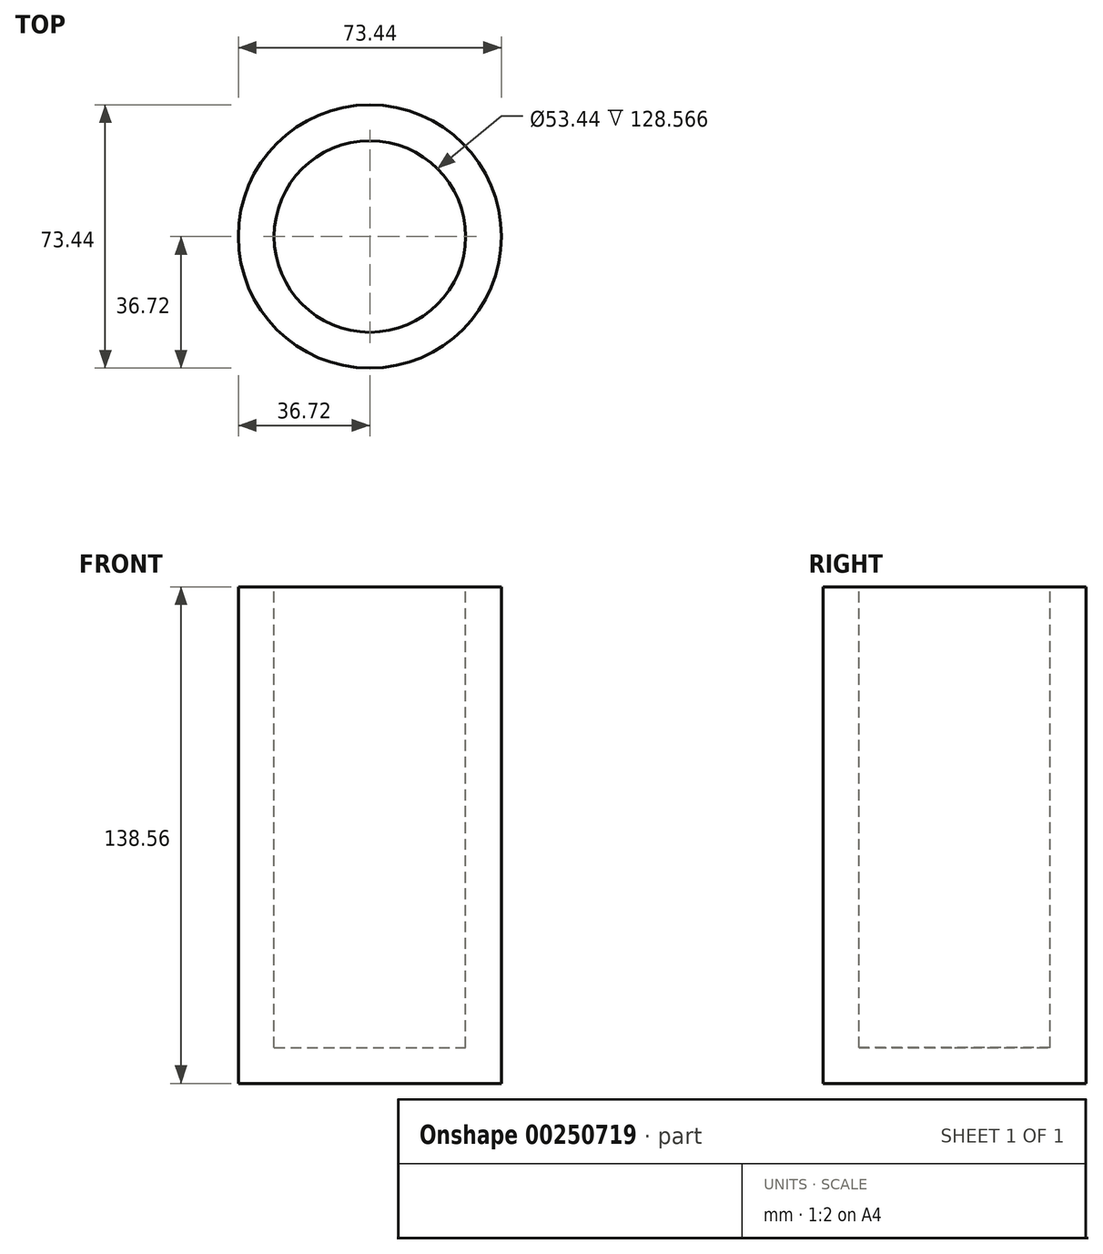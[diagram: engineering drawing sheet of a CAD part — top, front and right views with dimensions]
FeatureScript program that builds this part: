
annotation { "Feature Type Name" : "Feature", "Feature Type Description" : "" }
export const myFeature = defineFeature(function(context is Context, id is Id, definition is map)
    precondition{}
    {
        {
            var Q0;
            Q0=qCreatedBy(makeId("Front.planeOp"),FACE);
            var sketch = newSketch(context, id + "F0", { "sketchPlane" : qUnion([Q0])});
            skLineSegment(sketch, "E0.bottom", {"start": v(-36.72, 69.28) * mm, "end": v(36.72, 69.28) * mm});
            skLineSegment(sketch, "E0.top", {"start": v(-36.72, -69.28) * mm, "end": v(36.72, -69.28) * mm});
            skLineSegment(sketch, "E0.left", {"start": v(-36.72, 69.28) * mm, "end": v(-36.72, -69.28) * mm});
            skLineSegment(sketch, "E0.right", {"start": v(36.72, 69.28) * mm, "end": v(36.72, -69.28) * mm});
            skPoint(sketch, "E0.middle", {"position": v(0, 0) * mm});
            skLineSegment(sketch, "E1", {"start": v(0, 69.28) * mm, "end": v(0, -69.28) * mm});
            skSolve(sketch);
        }
        {
            var Q0;
            {var subQ0=sQuery(id+"F0.wireOp",EDGE,"E0.left");Q0=makeQuery(id+"F0.imprint","IMPRINT",FACE,{"disambiguationData":[TD([[makeQuery(id+"F0.imprint","IMPRINT",EDGE,{"derivedFrom":subQ0}),1.0]])]});}
            var Q1;
            Q1=sQuery(id+"F0.wireOp",EDGE,"E1");
            revolve(context, id + "F1", {"entities" : qUnion([Q0]), "axis" : qUnion([Q1]), "revolveType" : RevolveType.FULL});
        }
        {
            var Q0;
            Q0=makeQuery(id+"F1.opRevolve","SWEPT_FACE",FACE,{"disambiguationData":[OSD([sQuery(id+"F0.wireOp",EDGE,"E0.bottom")])]});
            var Q1;
            Q1=makeQuery(id+"F1.opRevolve","SWEPT_BODY",BODY,{"disambiguationData":[OSD([sQuery(id+"F0.wireOp",EDGE,"E0.bottom"),sQuery(id+"F0.wireOp",EDGE,"E0.top"),sQuery(id+"F0.wireOp",EDGE,"E0.left"),sQuery(id+"F0.wireOp",EDGE,"E1")])]});
            shell(context, id + "F2", {"entities" : qUnion([Q0]), "parts" : qUnion([Q1]), "thickness" : 10 * mm});
        }
    });
